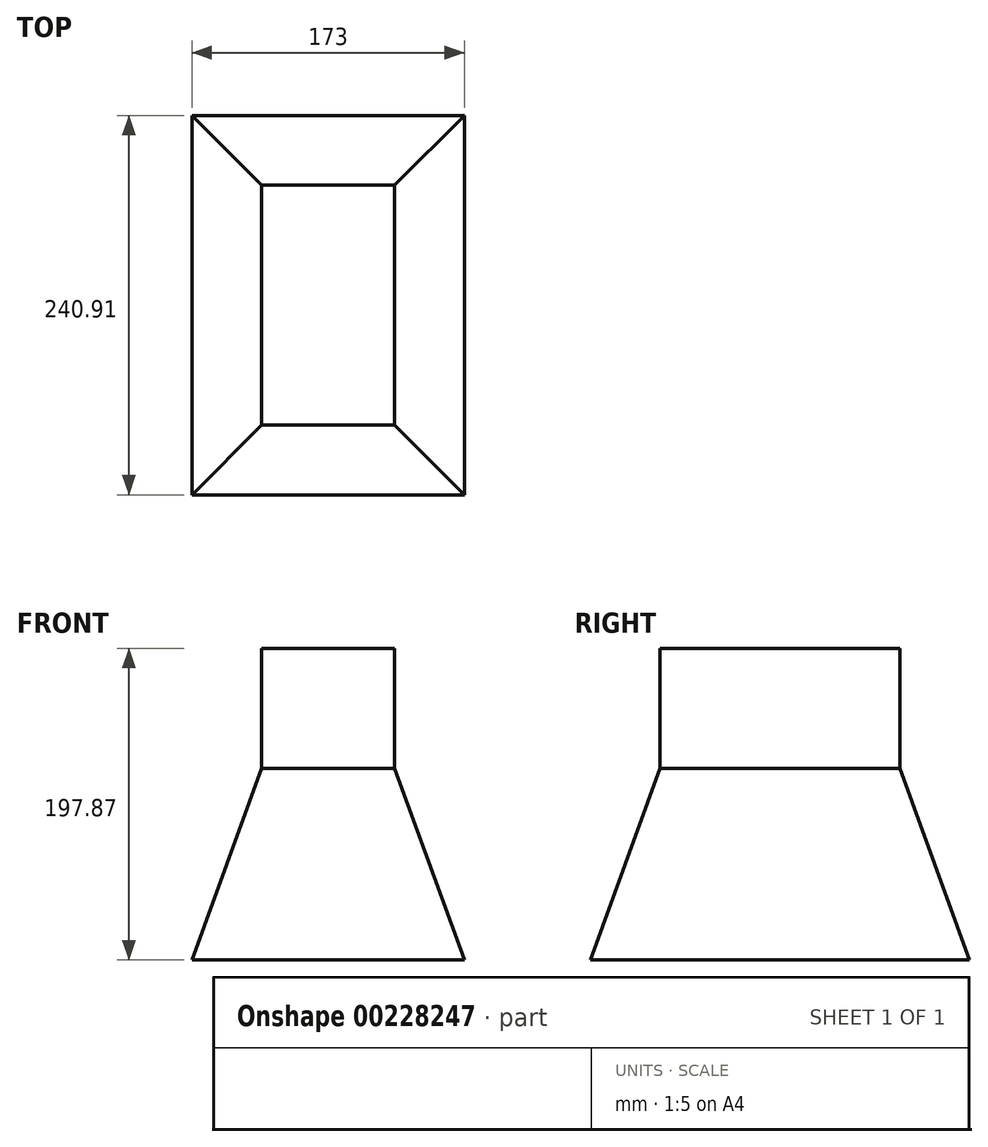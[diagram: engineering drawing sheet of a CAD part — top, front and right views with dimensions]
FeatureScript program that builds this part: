
annotation { "Feature Type Name" : "Feature", "Feature Type Description" : "" }
export const myFeature = defineFeature(function(context is Context, id is Id, definition is map)
    precondition{}
    {
        {
            var Q0;
            Q0=qCreatedBy(makeId("Top.planeOp"),FACE);
            var sketch = newSketch(context, id + "F0", { "sketchPlane" : qUnion([Q0])});
            skLineSegment(sketch, "E0.bottom", {"start": v(76, -76.32) * mm, "end": v(-8.43, -76.32) * mm});
            skLineSegment(sketch, "E0.top", {"start": v(76, 76.03) * mm, "end": v(-8.43, 76.03) * mm});
            skLineSegment(sketch, "E0.left", {"start": v(76, -76.32) * mm, "end": v(76, 76.03) * mm});
            skLineSegment(sketch, "E0.right", {"start": v(-8.43, -76.32) * mm, "end": v(-8.43, 76.03) * mm});
            skSolve(sketch);
        }
        {
            var Q0;
            Q0=makeQuery(id+"F0.imprint","IMPRINT",FACE,{"disambiguationData":[TD([[makeQuery(id+"F0.imprint","IMPRINT",EDGE,{"derivedFrom":sQuery(id+"F0.wireOp",EDGE,"E0.bottom")}),-1.0]])]});
            extrude(context, id + "F1", {"entities" : qUnion([Q0]), "depth" : 76.2 * mm, "hasSecondDirection" : true, "secondDirectionOppositeDirection" : true, "secondDirectionDepth" : 121.67 * mm, "hasSecondDirectionDraft" : true, "secondDirectionDraftAngle" : 20 * degree});
        }
    });
